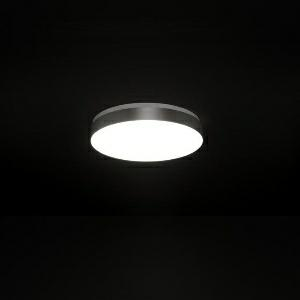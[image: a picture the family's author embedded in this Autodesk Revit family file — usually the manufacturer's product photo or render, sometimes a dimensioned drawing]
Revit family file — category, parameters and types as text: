
# Revit family: spectral_norea_norea-rp_416_4300_840_os_00af
name_source: partatom
category: Lighting Fixtures
revit_build: Autodesk Revit 2016 (Build: 20150220_1215(x64)
units: mm (PartAtom-declared; Revit-internal decimal feet)

## family parameters
Cut with Voids When Loaded = No
Host = Face
Light Source = No
Part Type = Normal
Room Calculation Point = No
Round Connector Dimension = Use Diameter
Shared = No

## types (1)
- SPECTRAL NOREA (1 x )
    Apparent Load = 0 VA
    Approval mark = CE
    CIE Flux Codes = 47 78 95 100 72
    Control Gear = Electronic transformer
    Default Elevation = 1800 mm
    Description = SPT0000137
NOREA Pendant luminaire

Round element with an opal acrylic panel in a natural anodised aluminium profile frame surround. The frame is fixed at the powder-coated metal body by a bayonet fixture with spring clip. The luminaire is suspended by a six trapezoidal wire pendants with ceiling fixture and transparent connecting cable round ceiling junction box. Cable length adjustable at the junction box, steel wire steplessly height adjustable. The metal body accommodates the electrical components and electronic ballast. The LED module is formed as a round LED flat board and can be removed for mounting or exchange using a keyhole screw connection. Plug-in electrical connection of the LED flat board. Luminaire with heat-resistant wiring. Homogenous illumination of the light surface. Suitable for ceiling or wall mounting. Also in a dimmable version. Protection rating IP20, safety class I.

Colour:
Housing – similar to RAL 9016 White silk matt;
Frame – natural anodised
    Height = 78 mm  [stored 0.255906 ft]
    Lamp = 1 x
    Lamp count = 1
    Length = 416 mm
    Luminous efficacy = 0 lm/W
    Manufacturer = Ridi
    ModVariant = No
    Model = NOREA-RP 416/4300/840 OS
    Mounting Place = Ceiling
    Mounting Type = Pendant
    Number of Poles = 1
    OnlyDefault = Yes
    Power Factor = 1
    Product Name = SPECTRAL NOREA
    Product group = Pendant luminaire
    ProductGroupID = 9
    Protection Class = Protection class
    Protection Degree = IP 20
    RlxData = <blob elided: 30129 chars, md5=3dc69466>
    Socket = socket
    Standby Power = 0 W
    System Light Flux = 0 lm
    System Power = 0 W
    Type Image = rundmittel01_-_kopie.jpg
    URL = http://reluxnet.relux.com
    VarID = 1
    Voltage = 0 V
    Weight = 0.00 kg
    Width = 0 mm  [stored 0 ft]

note: [stored X ft] marks values corroborated as IEEE doubles in the binary element streams (Revit-internal decimal feet)

## geometry (parser evidence)
native form markers: Sweep x9
no freeform markers — native parametric forms only
